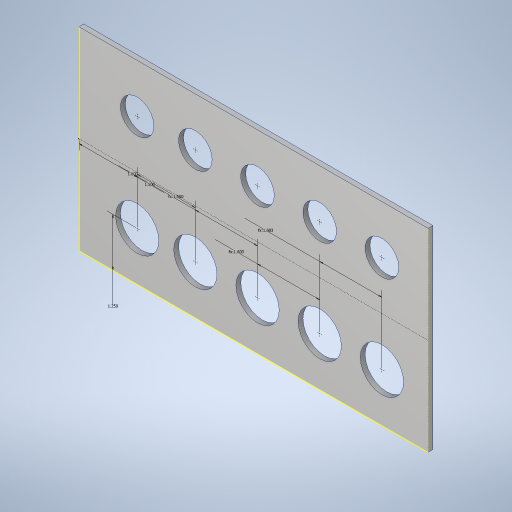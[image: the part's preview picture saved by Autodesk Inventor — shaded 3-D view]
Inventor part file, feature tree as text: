
AUTODESK INVENTOR PART (.ipt)
format: ipt  version: 2023.4 (Build 274418000, 418)  size: 284,160 bytes
history: native  units: in
note: dims shown in document units (in); Inventor stores cm internally (conversion verified against a paired STEP export)
features: hole x10, sketch x3, extrude x1
ambient origin geometry x8: Origin, YZ Plane, XZ Plane, XY Plane, X Axis, Y Axis, Z Axis, Center Point
bodies: Solid1 (feature_tree)
feature tree (14):
  extrude  "Extrusion1"  Depth=5.0in
  sketch  "Sketch2"  dims[d2=0.125in d3=0.0in d4=1.25in]
  hole  "Hole1"  [1 undecoded]
  hole  "Hole2"  [1 undecoded]
  hole  "Hole3"  [1 undecoded]
  hole  "Hole4"  [1 undecoded]
  hole  "Hole5"  [1 undecoded]
  sketch  "Sketch3"  dims[d5=1.5in d6=1.5in d7=1.603in d8=1.603in d9=1.603in d10=1.114in d11=0.75in d12=0.375in d13=0.25in d14=0.5635in d15=1.0in d16=0.8108in d17=1.115in d18=0.75in d19=0.375in d20=0.25in d21=0.5635in d22=1.0in d23=0.8108in d24=1.116in d25=0.75in d26=0.375in d27=0.25in d28=0.5635in d29=1.0in d30=0.8108in d31=1.117in d32=0.75in d33=0.375in d34=0.25in d35=0.5635in d36=1.0in d37=0.8108in d38=1.118in d39=0.75in d40=0.375in d41=0.25in d42=0.5635in d43=1.0in d44=0.8108in d45=0.865in d46=0.75in d47=0.375in d48=0.25in d49=0.5635in d50=1.0in d51=0.8108in d52=0.865in d53=0.75in d54=0.375in d55=0.25in d56=0.5635in d57=1.0in d58=0.8108in d59=0.866in d60=0.75in d61=0.375in d62=0.25in d63=0.5635in d64=1.0in d65=0.8108in d66=0.867in d67=0.75in d68=0.375in d69=0.25in d70=0.5635in d71=1.0in d72=0.8108in d73=0.868in d74=0.75in d75=0.375in d76=0.25in d77=0.5635in d78=1.0in d79=0.8108in]
  hole  "Hole6"  [1 undecoded]
  hole  "Hole7"  [1 undecoded]
  hole  "Hole8"  [1 undecoded]
  hole  "Hole9"  [1 undecoded]
  hole  "Hole10"  [1 undecoded]
  sketch  "Sketch1"  dims[d0=9.0in d1=5.0in]
note: 10 required parameter values undecoded (feature->parameter linkage not recoverable at this tier; creation-order binding heuristic only, values carry confidence <= 0.55)
